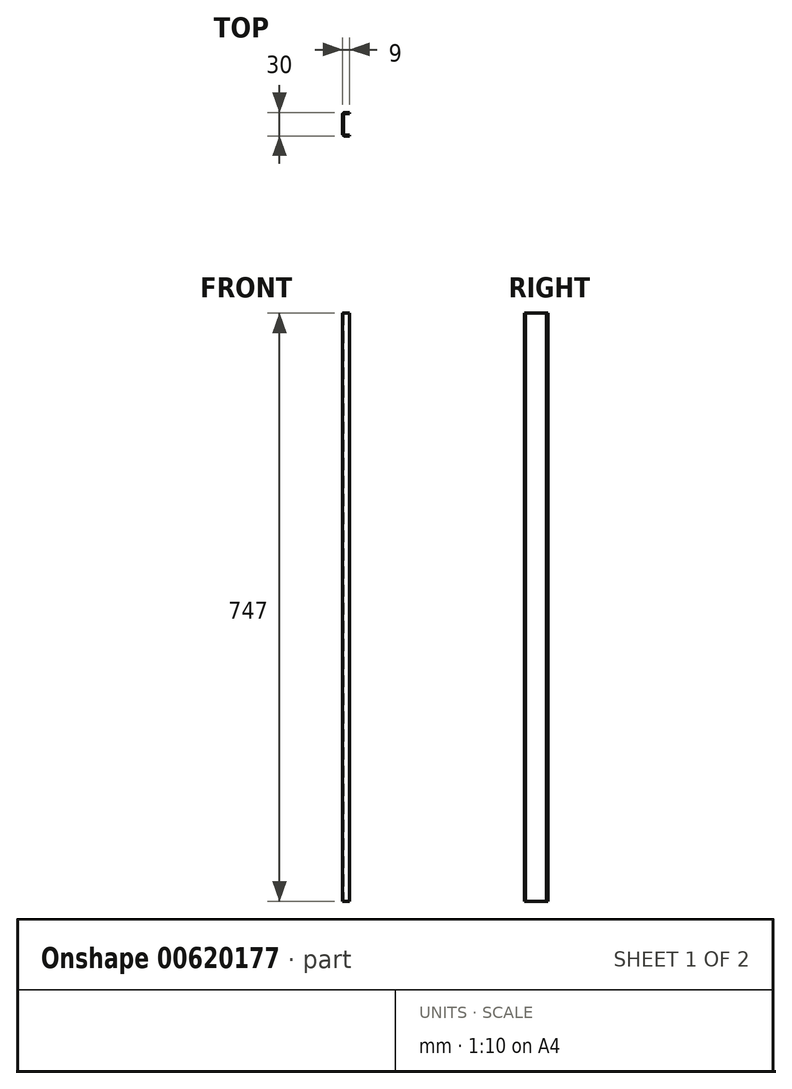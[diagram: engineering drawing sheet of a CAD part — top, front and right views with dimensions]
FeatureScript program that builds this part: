
annotation { "Feature Type Name" : "Feature", "Feature Type Description" : "" }
export const myFeature = defineFeature(function(context is Context, id is Id, definition is map)
    precondition{}
    {
        {
            var Q0;
            Q0=qCreatedBy(makeId("Top.planeOp"),FACE);
            var sketch = newSketch(context, id + "F0", { "sketchPlane" : qUnion([Q0])});
            skLineSegment(sketch, "E0", {"start": v(0, 0) * mm, "end": v(0, 12) * mm});
            skLineSegment(sketch, "E1", {"start": v(3, 15) * mm, "end": v(9, 15) * mm});
            skPoint(sketch, "E2.visualSharp", {"position": v(0, 15) * mm});
            skArc(sketch, "E2.filletArc", {"start": v(3, 15) * mm, "mid": v(0.88, 14.12) * mm, "end": v(0, 12) * mm});
            skLineSegment(sketch, "E3.0", {"start": v(3, 13.5) * mm, "end": v(9, 13.5) * mm});
            skArc(sketch, "E3.1", {"start": v(3, 13.5) * mm, "mid": v(1.94, 13.06) * mm, "end": v(1.5, 12) * mm});
            skLineSegment(sketch, "E3.2", {"start": v(1.5, 0) * mm, "end": v(1.5, 12) * mm});
            skLineSegment(sketch, "E4", {"start": v(9, 15) * mm, "end": v(9, 13.5) * mm});
            skLineSegment(sketch, "E5.MirrorCS", {"start": v(0, 0) * mm, "end": v(0, -12) * mm});
            skArc(sketch, "E6.MirrorCS", {"start": v(3, -15) * mm, "mid": v(0.88, -14.12) * mm, "end": v(0, -12) * mm});
            skLineSegment(sketch, "E7.MirrorCS", {"start": v(3, -15) * mm, "end": v(9, -15) * mm});
            skLineSegment(sketch, "E8.MirrorCS", {"start": v(9, -15) * mm, "end": v(9, -13.5) * mm});
            skLineSegment(sketch, "E9.MirrorCS", {"start": v(3, -13.5) * mm, "end": v(9, -13.5) * mm});
            skArc(sketch, "E10.MirrorCS", {"start": v(3, -13.5) * mm, "mid": v(1.94, -13.06) * mm, "end": v(1.5, -12) * mm});
            skLineSegment(sketch, "E11.MirrorCS", {"start": v(1.5, 0) * mm, "end": v(1.5, -12) * mm});
            skSolve(sketch);
        }
        {
            var Q0;
            Q0=makeQuery(id+"F0.imprint","IMPRINT",FACE,{"disambiguationData":[TD([[makeQuery(id+"F0.imprint","IMPRINT",EDGE,{"derivedFrom":sQuery(id+"F0.wireOp",EDGE,"E0")}),-1.0]])]});
            extrude(context, id + "F1", {"entities" : qUnion([Q0]), "depth" : 747 * mm, "offsetDistance" : 25 * mm});
        }
    });
